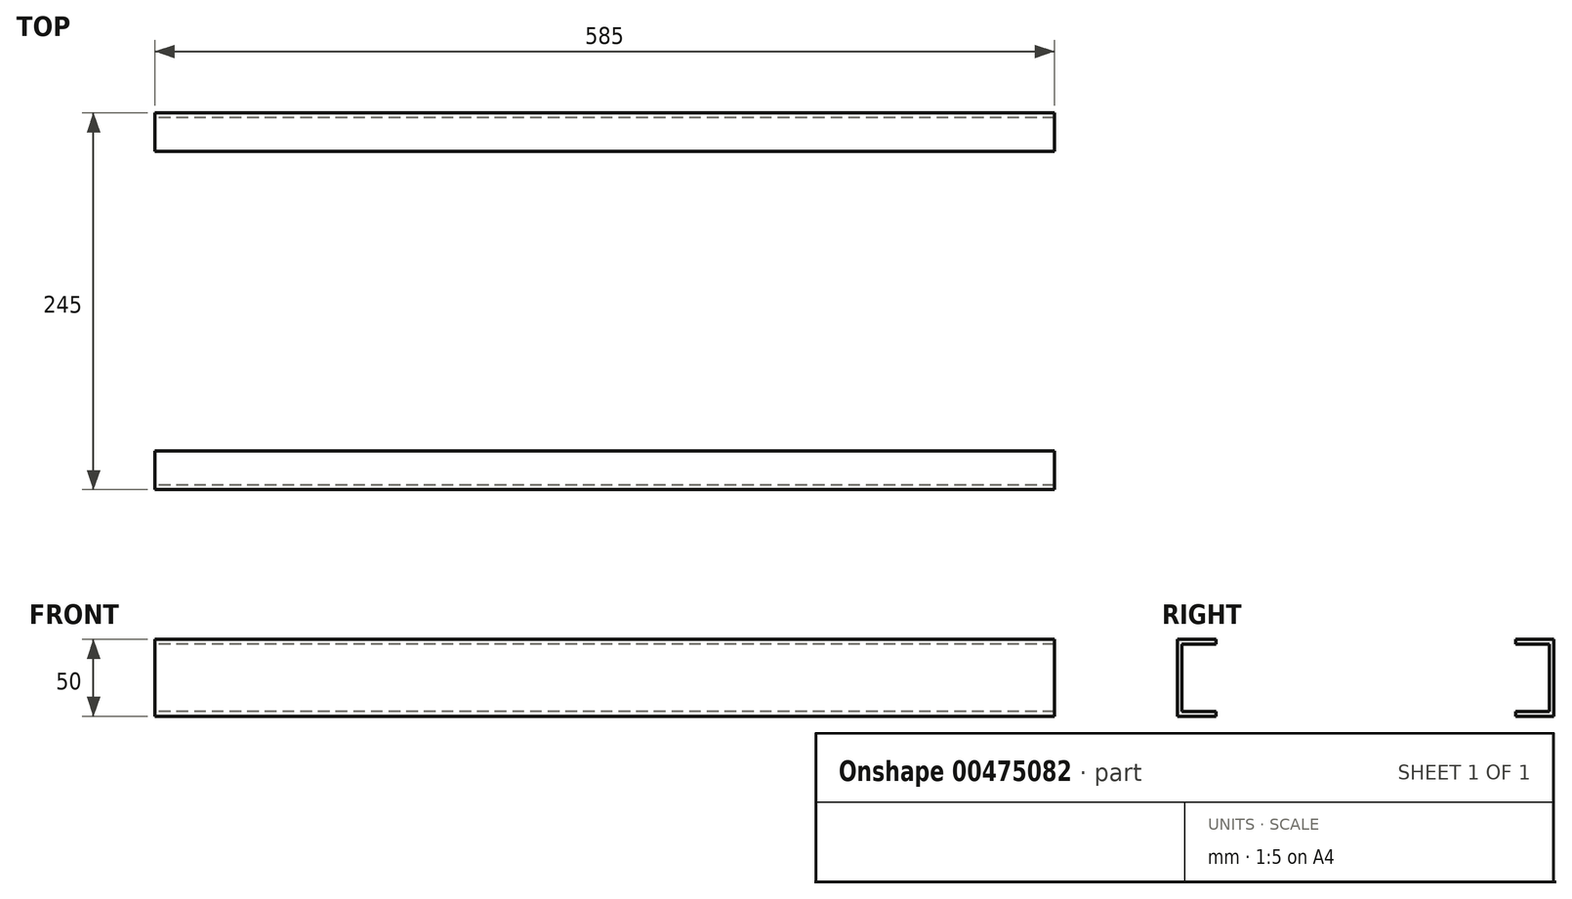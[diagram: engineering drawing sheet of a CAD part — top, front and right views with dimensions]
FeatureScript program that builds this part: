
annotation { "Feature Type Name" : "Feature", "Feature Type Description" : "" }
export const myFeature = defineFeature(function(context is Context, id is Id, definition is map)
    precondition{}
    {
        {
            var Q0;
            Q0=qCreatedBy(makeId("Right.planeOp"),FACE);
            var sketch = newSketch(context, id + "F0", { "sketchPlane" : qUnion([Q0])});
            skLineSegment(sketch, "E0", {"start": v(0, 127.17) * mm, "end": v(0, -96.2) * mm, "construction": true});
            skLineSegment(sketch, "E1", {"start": v(-122.5, -30.98) * mm, "end": v(-122.5, -80.98) * mm});
            skLineSegment(sketch, "E2", {"start": v(-122.5, -80.98) * mm, "end": v(-97.5, -80.98) * mm});
            skLineSegment(sketch, "E3", {"start": v(-97.5, -80.98) * mm, "end": v(-97.5, -77.98) * mm});
            skLineSegment(sketch, "E4", {"start": v(-97.5, -77.98) * mm, "end": v(-119.5, -77.98) * mm});
            skLineSegment(sketch, "E5", {"start": v(-119.5, -77.98) * mm, "end": v(-119.5, -33.98) * mm});
            skLineSegment(sketch, "E6", {"start": v(-119.5, -33.98) * mm, "end": v(-97.5, -33.98) * mm});
            skLineSegment(sketch, "E7", {"start": v(-122.5, -30.98) * mm, "end": v(-97.5, -30.98) * mm});
            skLineSegment(sketch, "E8", {"start": v(-97.5, -30.98) * mm, "end": v(-97.5, -33.98) * mm});
            skLineSegment(sketch, "E9", {"start": v(97.5, -80.98) * mm, "end": v(122.5, -80.98) * mm});
            skLineSegment(sketch, "E10", {"start": v(122.5, -80.98) * mm, "end": v(122.5, -30.98) * mm});
            skLineSegment(sketch, "E11", {"start": v(122.5, -30.98) * mm, "end": v(97.5, -30.98) * mm});
            skLineSegment(sketch, "E12", {"start": v(97.5, -30.98) * mm, "end": v(97.5, -33.98) * mm});
            skLineSegment(sketch, "E13", {"start": v(97.5, -33.98) * mm, "end": v(119.5, -33.98) * mm});
            skLineSegment(sketch, "E14", {"start": v(119.5, -33.98) * mm, "end": v(119.5, -77.98) * mm});
            skLineSegment(sketch, "E15", {"start": v(119.5, -77.98) * mm, "end": v(97.5, -77.98) * mm});
            skLineSegment(sketch, "E16", {"start": v(97.5, -77.98) * mm, "end": v(97.5, -80.98) * mm});
            skSolve(sketch);
        }
        {
            var Q0;
            Q0=makeQuery(id+"F0.imprint","IMPRINT",FACE,{"disambiguationData":[TD([[makeQuery(id+"F0.imprint","IMPRINT",EDGE,{"derivedFrom":sQuery(id+"F0.wireOp",EDGE,"E1")}),1.0]])]});
            var Q1;
            Q1=makeQuery(id+"F0.imprint","IMPRINT",FACE,{"disambiguationData":[TD([[makeQuery(id+"F0.imprint","IMPRINT",EDGE,{"derivedFrom":sQuery(id+"F0.wireOp",EDGE,"E9")}),1.0]])]});
            extrude(context, id + "F1", {"entities" : qUnion([Q0, Q1]), "endBound" : BoundingType.SYMMETRIC, "depth" : 585 * mm});
        }
    });
